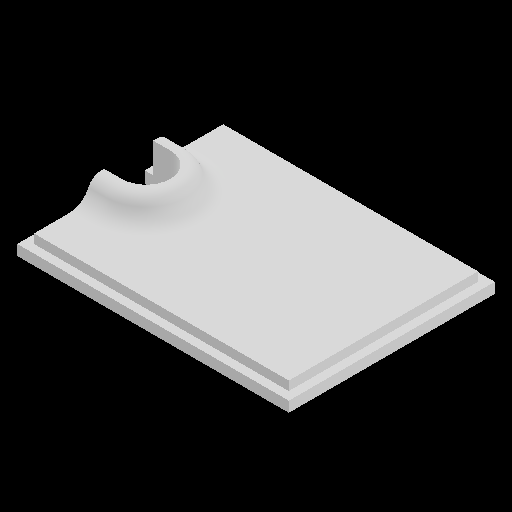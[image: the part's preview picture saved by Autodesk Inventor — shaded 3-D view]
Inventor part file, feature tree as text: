
AUTODESK INVENTOR PART (.ipt)
format: ipt  version: 2023 (Build 270158000, 158)  size: 100,864 bytes
history: native  units: mm
features: fillet x1
ambient origin geometry x8: Origin, YZ Plane, XZ Plane, XY Plane, X Axis, Y Axis, Z Axis, Center Point
bodies: Solid1 (feature_tree)
feature tree (1):
  fillet  "Fillet2"  [1 undecoded]
note: 1 required parameter value undecoded (feature->parameter linkage not recoverable at this tier; creation-order binding heuristic only, values carry confidence <= 0.55)
